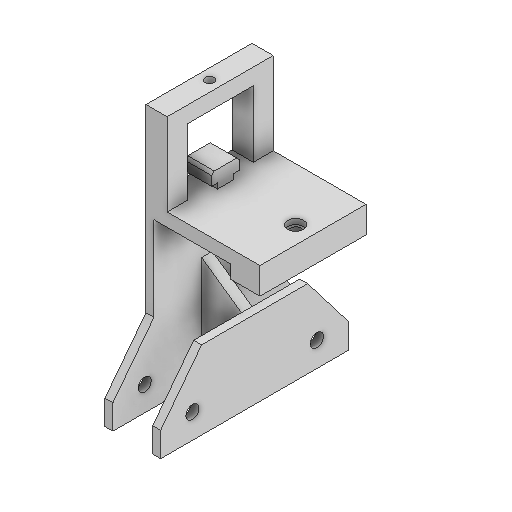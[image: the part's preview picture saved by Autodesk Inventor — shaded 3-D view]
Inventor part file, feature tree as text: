
AUTODESK INVENTOR PART (.ipt)
format: ipt  version: 2025.1 (Build 291241000, 241)  size: 246,784 bytes
history: native  units: mm
features: sketch x13, extrude x10, hole x3, other x1, chamfer x1
ambient origin geometry x8: Origin, YZ Plane, XZ Plane, XY Plane, X Axis, Y Axis, Z Axis, Center Point
bodies: Body1 (feature_tree)
feature tree (28):
  other  "Bryła1"
  extrude  "Wyciągnięcie proste1"  Depth=25.0mm
  hole  "Otwór1"  [1 undecoded]
  extrude  "Wyciągnięcie proste2"  Depth=82.089mm
  extrude  "Wyciągnięcie proste3"  Depth=20.0mm
  extrude  "Wyciągnięcie proste4"  Depth=3.0mm TaperAngle=0.0deg
  chamfer  "Faza1"  Distance=82.089mm
  extrude  "Wyciągnięcie proste5"  Depth=82.089mm
  hole  "Otwór3"  [1 undecoded]
  extrude  "Wyciągnięcie proste6"  Depth=12.0mm
  extrude  "Wyciągnięcie proste7"  Depth=5.0mm TaperAngle=0.0deg
  hole  "Otwór4"  [1 undecoded]
  extrude  "Wyciągnięcie proste8"  Depth=40.0mm
  extrude  "Wyciągnięcie proste9"  Depth=4.0mm
  extrude  "Wyciągnięcie proste10"  Depth=15.0mm TaperAngle=0.0deg
  sketch  "Szkic1"
  sketch  "Szkic2"
  sketch  "Szkic3"
  sketch  "Szkic5"
  sketch  "Szkic6"
  sketch  "Szkic7"
  sketch  "Szkic8"
  sketch  "Szkic9"
  sketch  "Szkic10"
  sketch  "Szkic11"
  sketch  "Szkic13"
  sketch  "Szkic14"
  sketch  "Szkic15"
note: 3 required parameter values undecoded (feature->parameter linkage not recoverable at this tier; creation-order binding heuristic only, values carry confidence <= 0.55)
